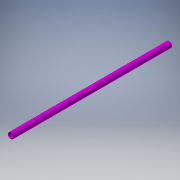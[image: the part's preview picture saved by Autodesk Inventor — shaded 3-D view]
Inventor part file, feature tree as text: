
AUTODESK INVENTOR PART (.ipt)
format: ipt  version: 2018 (Build 220112000, 112)  size: 106,496 bytes
history: native  units: in
note: dims shown in document units (in); Inventor stores cm internally (conversion verified against a paired STEP export)
features: extrude x1, sketch x1
ambient origin geometry x8: Origin, YZ Plane, XZ Plane, XY Plane, X Axis, Y Axis, Z Axis, Center Point
bodies: Solid1 (feature_tree)
feature tree (2):
  extrude  "Extrusion1"  Depth=35.556in
  sketch  "Sketch1"  dims[d0=1.315in d1=1.0in d2=35.556in d3=0.0in]
